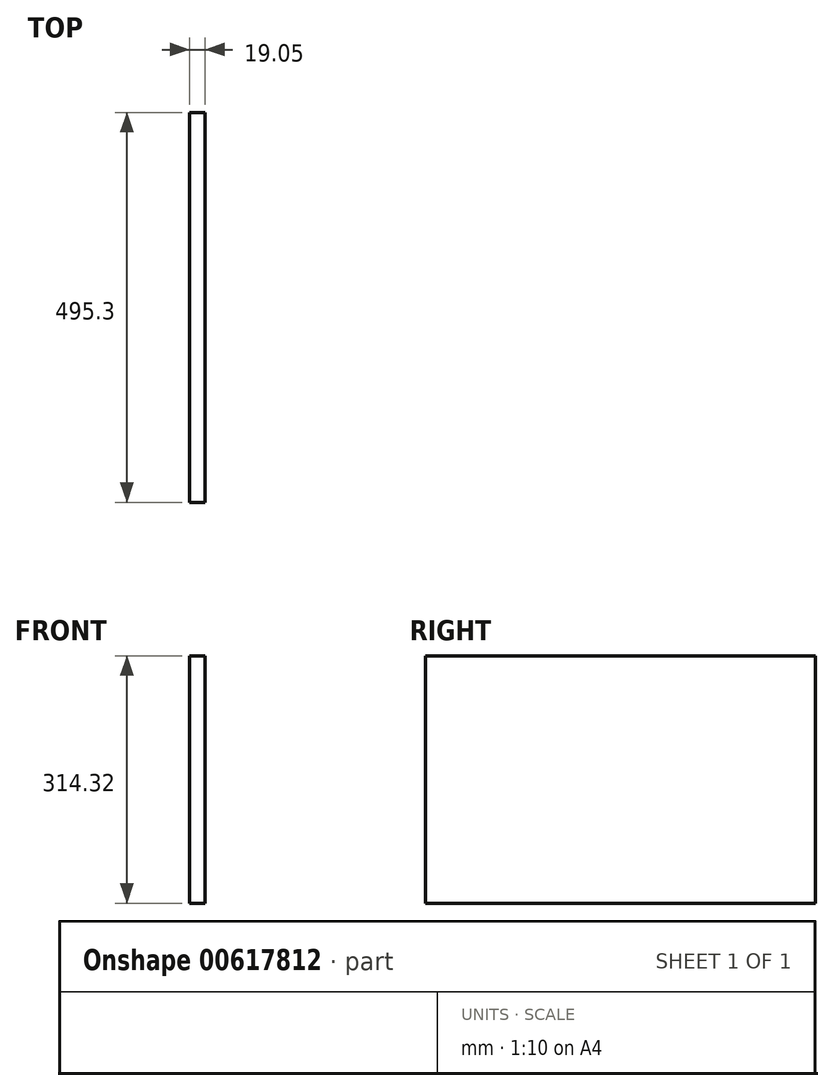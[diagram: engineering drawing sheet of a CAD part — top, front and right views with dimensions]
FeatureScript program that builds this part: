
annotation { "Feature Type Name" : "Feature", "Feature Type Description" : "" }
export const myFeature = defineFeature(function(context is Context, id is Id, definition is map)
    precondition{}
    {
        {
            var Q0;
            Q0=qCreatedBy(makeId("Right.planeOp"),FACE);
            var sketch = newSketch(context, id + "F0", { "sketchPlane" : qUnion([Q0])});
            skLineSegment(sketch, "E0.bottom", {"start": v(247.65, 157.16) * mm, "end": v(-247.65, 157.16) * mm});
            skLineSegment(sketch, "E0.top", {"start": v(247.65, -157.16) * mm, "end": v(-247.65, -157.16) * mm});
            skLineSegment(sketch, "E0.left", {"start": v(247.65, 157.16) * mm, "end": v(247.65, -157.16) * mm});
            skLineSegment(sketch, "E0.right", {"start": v(-247.65, 157.16) * mm, "end": v(-247.65, -157.16) * mm});
            skPoint(sketch, "E0.middle", {"position": v(0, 0) * mm});
            skSolve(sketch);
        }
        {
            var Q0;
            Q0=makeQuery(id+"F0.imprint","IMPRINT",FACE,{"disambiguationData":[TD([[makeQuery(id+"F0.imprint","IMPRINT",EDGE,{"derivedFrom":sQuery(id+"F0.wireOp",EDGE,"E0.bottom")}),1.0]])]});
            extrude(context, id + "F1", {"entities" : qUnion([Q0]), "depth" : 19.05 * mm, "offsetDistance" : 25.4 * mm});
        }
    });
